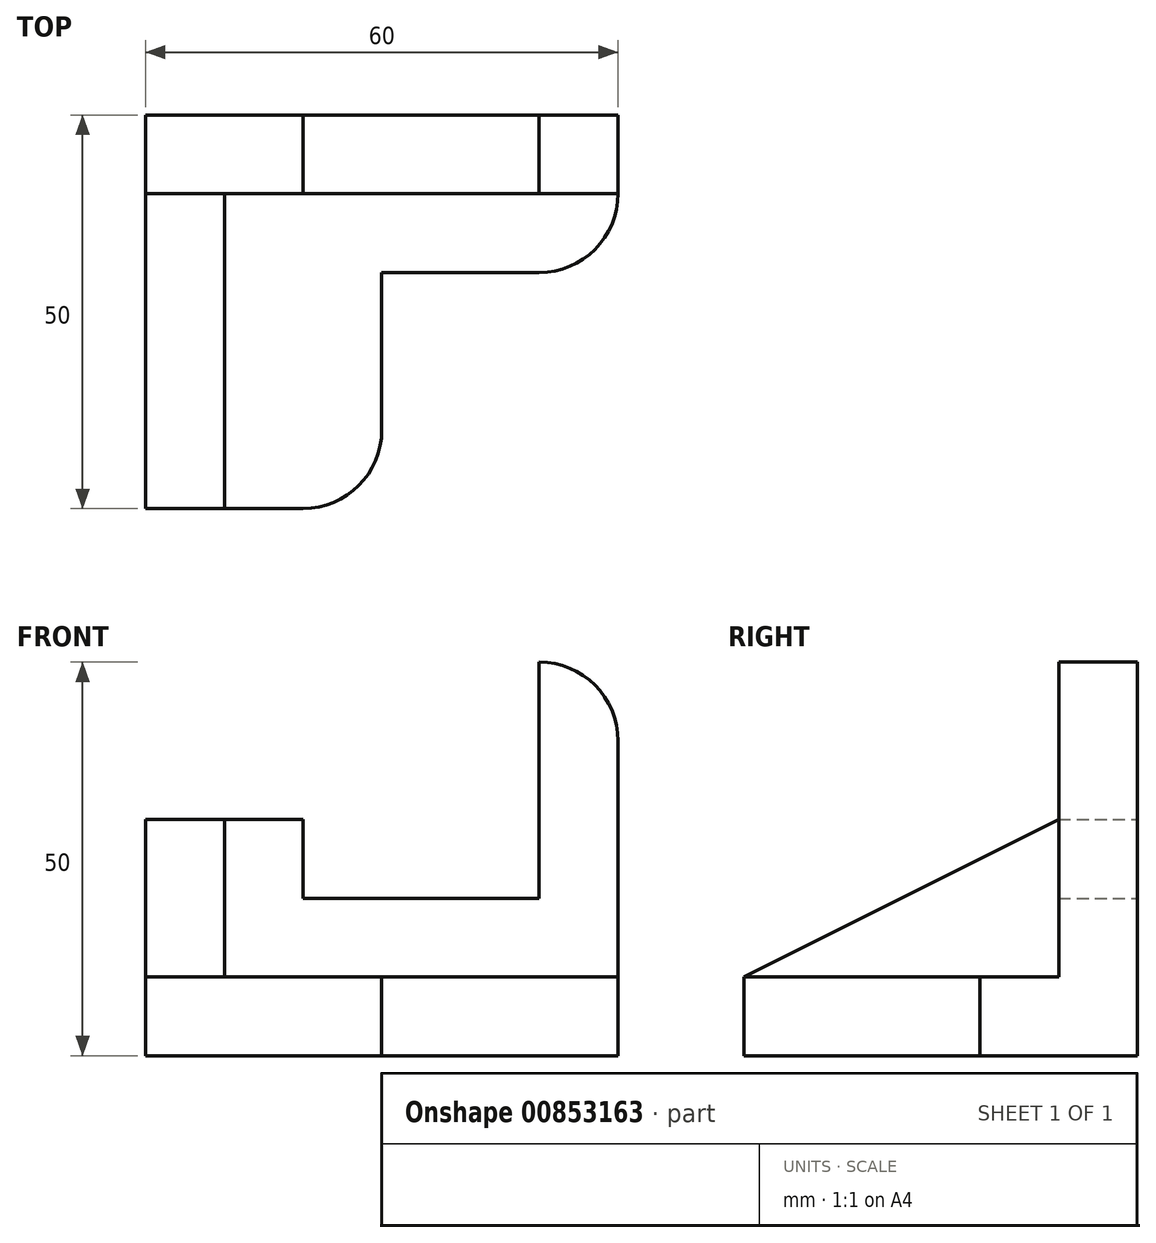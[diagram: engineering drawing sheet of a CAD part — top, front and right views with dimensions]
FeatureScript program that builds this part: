
annotation { "Feature Type Name" : "Feature", "Feature Type Description" : "" }
export const myFeature = defineFeature(function(context is Context, id is Id, definition is map)
    precondition{}
    {
        {
            var Q0;
            Q0=qCreatedBy(makeId("Top.planeOp"),FACE);
            var sketch = newSketch(context, id + "F0", { "sketchPlane" : qUnion([Q0])});
            skLineSegment(sketch, "E0", {"start": v(0, 15.04) * mm, "end": v(0, -34.96) * mm});
            skLineSegment(sketch, "E1", {"start": v(0, 15.04) * mm, "end": v(60, 15.04) * mm});
            skLineSegment(sketch, "E2", {"start": v(0, -34.96) * mm, "end": v(20, -34.96) * mm});
            skLineSegment(sketch, "E3", {"start": v(30, -24.96) * mm, "end": v(30, -4.96) * mm});
            skLineSegment(sketch, "E4", {"start": v(30, -4.96) * mm, "end": v(50, -4.96) * mm});
            skLineSegment(sketch, "E5", {"start": v(60, 5.04) * mm, "end": v(60, 15.04) * mm});
            skPoint(sketch, "E6.visualSharp", {"position": v(60, -4.96) * mm});
            skArc(sketch, "E6.filletArc", {"start": v(50, -4.96) * mm, "mid": v(57.07, -2.03) * mm, "end": v(60, 5.04) * mm});
            skPoint(sketch, "E7.visualSharp", {"position": v(30, -34.96) * mm});
            skArc(sketch, "E7.filletArc", {"start": v(20, -34.96) * mm, "mid": v(27.07, -32.03) * mm, "end": v(30, -24.96) * mm});
            skSolve(sketch);
        }
        {
            var Q0;
            Q0 = qSketchRegion(id + "F0", true);
            extrude(context, id + "F1", {"entities" : qUnion([Q0]), "depth" : 10 * mm, "offsetDistance" : 25 * mm});
        }
        {
            var Q0;
            Q0=makeQuery(id+"F1.opExtrude","SWEPT_FACE",FACE,{"disambiguationData":[OSD([sQuery(id+"F0.wireOp",EDGE,"E1")])]});
            var sketch = newSketch(context, id + "F2", { "sketchPlane" : qUnion([Q0])});
            skLineSegment(sketch, "E8", {"start": v(-60, 10) * mm, "end": v(-60, 40) * mm});
            skLineSegment(sketch, "E9", {"start": v(0, 30) * mm, "end": v(0, 10) * mm});
            skPoint(sketch, "E10.visualSharp", {"position": v(-60, 50) * mm});
            skArc(sketch, "E10.filletArc", {"start": v(-50, 50) * mm, "mid": v(-57.07, 47.07) * mm, "end": v(-60, 40) * mm});
            skLineSegment(sketch, "E11", {"start": v(0, 30) * mm, "end": v(-20, 30) * mm});
            skLineSegment(sketch, "E12", {"start": v(-20, 30) * mm, "end": v(-20, 20) * mm});
            skLineSegment(sketch, "E13", {"start": v(-20, 20) * mm, "end": v(-50, 20) * mm});
            skLineSegment(sketch, "E14", {"start": v(-50, 20) * mm, "end": v(-50, 50) * mm});
            skSolve(sketch);
        }
        {
            var Q0;
            Q0 = qSketchRegion(id + "F2", true);
            var Q1;
            Q1=makeQuery(id+"F2.imprint","IMPRINT",FACE,{"disambiguationData":[TD([[makeQuery(id+"F2.imprint","IMPRINT",EDGE,{"derivedFrom":sQuery(id+"F2.wireOp",EDGE,"E8")}),-1.0]])]});
            extrude(context, id + "F3", {"entities" : qUnion([Q0, Q1]), "operationType" : NewBodyOperationType.ADD, "depth" : -10 * mm, "offsetDistance" : 25 * mm});
        }
        {
            var Q0;
            Q0=makeQuery(id+"F1.opExtrude","CAP_FACE",FACE,{"disambiguationData":[OSD([sQuery(id+"F0.wireOp",EDGE,"E0"),sQuery(id+"F0.wireOp",EDGE,"E1"),sQuery(id+"F0.wireOp",EDGE,"E2"),sQuery(id+"F0.wireOp",EDGE,"E3"),sQuery(id+"F0.wireOp",EDGE,"E4"),sQuery(id+"F0.wireOp",EDGE,"E5"),sQuery(id+"F0.wireOp",EDGE,"E6.filletArc"),sQuery(id+"F0.wireOp",EDGE,"E7.filletArc")])],"isStart":false});
            var sketch = newSketch(context, id + "F4", { "sketchPlane" : qUnion([Q0])});
            skLineSegment(sketch, "E15.bottom", {"start": v(0, -34.96) * mm, "end": v(10, -34.96) * mm});
            skLineSegment(sketch, "E15.top", {"start": v(0, 5.04) * mm, "end": v(10, 5.04) * mm});
            skLineSegment(sketch, "E15.left", {"start": v(0, -34.96) * mm, "end": v(0, 5.04) * mm});
            skLineSegment(sketch, "E15.right", {"start": v(10, -34.96) * mm, "end": v(10, 5.04) * mm});
            skSolve(sketch);
        }
        {
            var Q0;
            Q0 = qSketchRegion(id + "F4", true);
            extrude(context, id + "F5", {"entities" : qUnion([Q0]), "operationType" : NewBodyOperationType.ADD, "depth" : 20 * mm, "offsetDistance" : 25 * mm});
        }
        {
            var Q0;
            Q0=makeQuery(id+"F5.opExtrude","CAP_EDGE",EDGE,{"disambiguationData":[OSD([sQuery(id+"F4.wireOp",EDGE,"E15.bottom")])],"isStart":false});
            chamfer(context, id + "F6", {"entities" : qUnion([Q0]), "chamferType" : ChamferType.TWO_OFFSETS, "width1" : 40 * mm, "oppositeDirection" : false, "width2" : 20 * mm, "tangentPropagation" : true});
        }
    });
